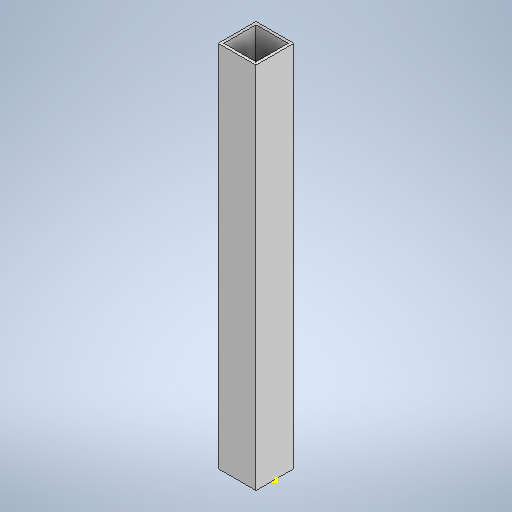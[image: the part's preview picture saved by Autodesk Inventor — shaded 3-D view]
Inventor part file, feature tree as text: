
AUTODESK INVENTOR PART (.ipt)
format: ipt  version: 2025 (Build 290162000, 162)  size: 250,368 bytes
history: native  units: in
note: dims shown in document units (in); Inventor stores cm internally (conversion verified against a paired STEP export)
features: sketch x2, extrude x1
ambient origin geometry x8: Origin, YZ Plane, XZ Plane, XY Plane, X Axis, Y Axis, Z Axis, Center Point
bodies: Solid1 (feature_tree)
feature tree (3):
  extrude  "Extrusion1"  Depth=1.5748in
  sketch  "Sketch2"  dims[d2=1.3386in d3=1.3386in d4=0.1181in d5=15.3543in d6=0.0in]
  sketch  "Sketch1"  dims[d0=1.5748in d1=1.5748in]
